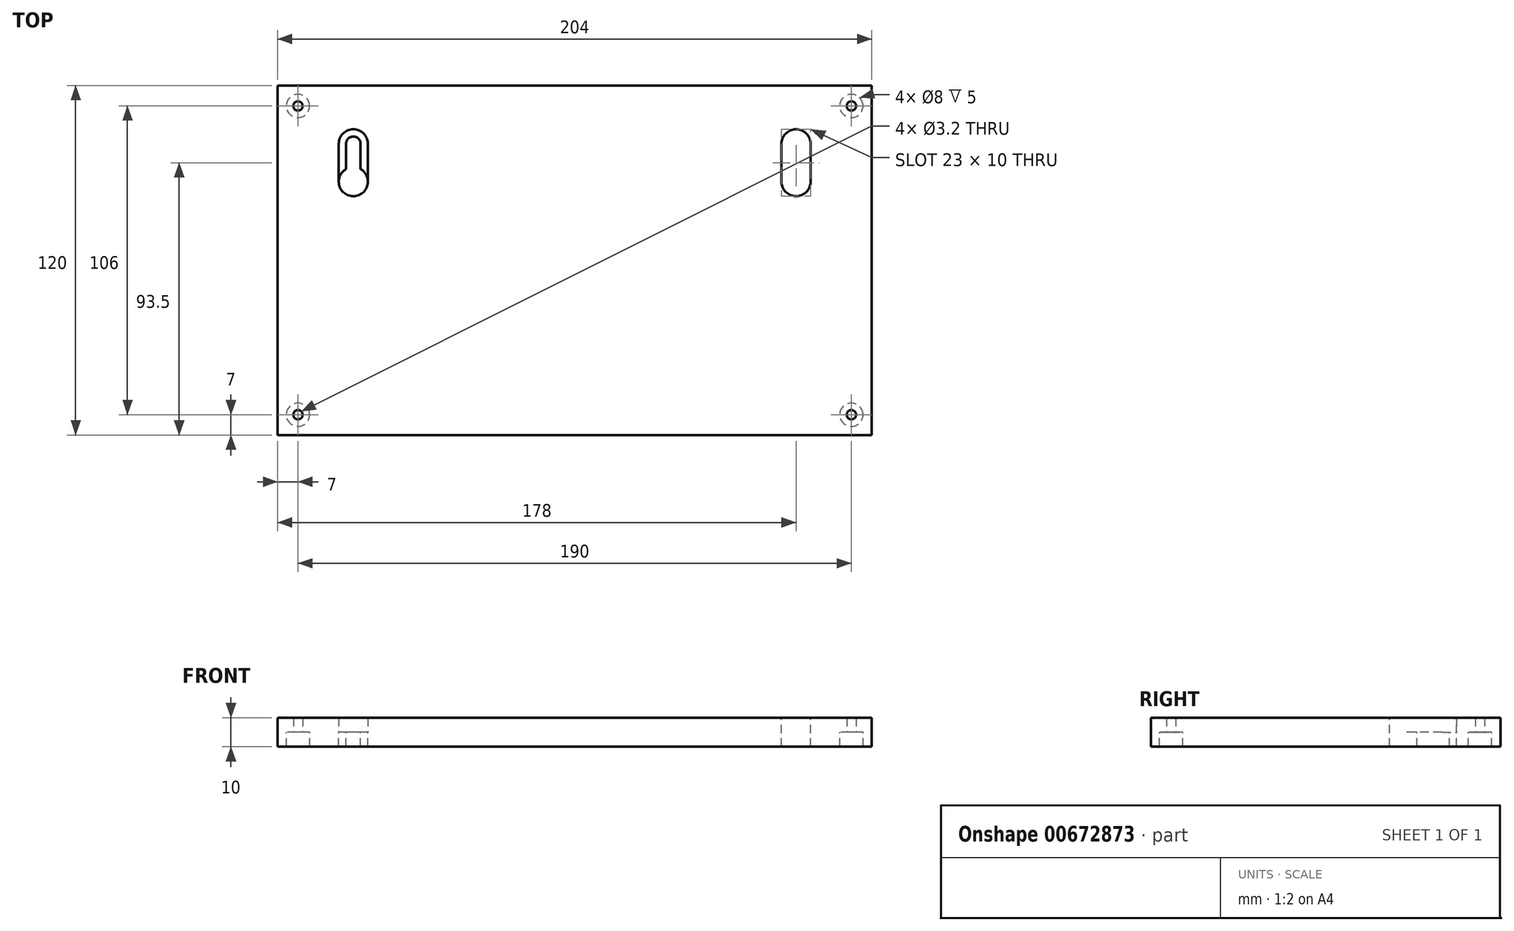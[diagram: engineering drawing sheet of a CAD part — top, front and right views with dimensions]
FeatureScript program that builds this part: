
annotation { "Feature Type Name" : "Feature", "Feature Type Description" : "" }
export const myFeature = defineFeature(function(context is Context, id is Id, definition is map)
    precondition{}
    {
        {
            var Q0;
            Q0=qCreatedBy(makeId("Top.planeOp"),FACE);
            var sketch = newSketch(context, id + "F0", { "sketchPlane" : qUnion([Q0])});
            skLineSegment(sketch, "E0.bottom", {"start": v(102, 60) * mm, "end": v(-102, 60) * mm});
            skLineSegment(sketch, "E0.top", {"start": v(102, -60) * mm, "end": v(-102, -60) * mm});
            skLineSegment(sketch, "E0.left", {"start": v(102, 60) * mm, "end": v(102, -60) * mm});
            skLineSegment(sketch, "E0.right", {"start": v(-102, 60) * mm, "end": v(-102, -60) * mm});
            skPoint(sketch, "E0.middle", {"position": v(0, 0) * mm});
            skArc(sketch, "E1", {"start": v(-71, 40) * mm, "mid": v(-76, 45) * mm, "end": v(-81, 40) * mm});
            skLineSegment(sketch, "E2", {"start": v(-81, 40) * mm, "end": v(-81, 27) * mm});
            skLineSegment(sketch, "E3", {"start": v(-71, 40) * mm, "end": v(-71, 27) * mm});
            skArc(sketch, "E4", {"start": v(-81, 27) * mm, "mid": v(-76, 22) * mm, "end": v(-71, 27) * mm});
            skArc(sketch, "E5", {"start": v(-78.5, 40) * mm, "mid": v(-76, 42.5) * mm, "end": v(-73.5, 40) * mm});
            skArc(sketch, "E6", {"start": v(-71, 27) * mm, "mid": v(-71.67, 29.5) * mm, "end": v(-73.5, 31.33) * mm});
            skLineSegment(sketch, "E7", {"start": v(-78.5, 40) * mm, "end": v(-78.5, 31.33) * mm});
            skLineSegment(sketch, "E8", {"start": v(-73.5, 40) * mm, "end": v(-73.5, 31.33) * mm});
            skArc(sketch, "E9.trimOffspring", {"start": v(-78.5, 31.33) * mm, "mid": v(-80.33, 29.5) * mm, "end": v(-81, 27) * mm});
            skArc(sketch, "E10", {"start": v(71, 40) * mm, "mid": v(76, 45) * mm, "end": v(81, 40) * mm});
            skLineSegment(sketch, "E11", {"start": v(71, 40) * mm, "end": v(71, 27) * mm});
            skLineSegment(sketch, "E12", {"start": v(81, 40) * mm, "end": v(81, 27) * mm});
            skArc(sketch, "E13", {"start": v(71, 27) * mm, "mid": v(76, 22) * mm, "end": v(81, 27) * mm});
            skArc(sketch, "E14", {"start": v(73.5, 40) * mm, "mid": v(76, 42.5) * mm, "end": v(78.5, 40) * mm});
            skArc(sketch, "E15", {"start": v(81, 27) * mm, "mid": v(80.33, 29.5) * mm, "end": v(78.5, 31.33) * mm});
            skLineSegment(sketch, "E16", {"start": v(73.5, 40) * mm, "end": v(73.5, 31.33) * mm});
            skLineSegment(sketch, "E17", {"start": v(78.5, 40) * mm, "end": v(78.5, 31.33) * mm});
            skArc(sketch, "E18.trimOffspring", {"start": v(73.5, 31.33) * mm, "mid": v(71.67, 29.5) * mm, "end": v(71, 27) * mm});
            skLineSegment(sketch, "E19.bottom", {"start": v(102, 60) * mm, "end": v(95, 60) * mm});
            skLineSegment(sketch, "E19.top", {"start": v(96.6, 53) * mm, "end": v(95, 53) * mm});
            skLineSegment(sketch, "E19.left", {"start": v(102, 60) * mm, "end": v(102, 53) * mm});
            skCircle(sketch, "E20", {"center": v(95, 53) * mm, "radius": 4 * mm});
            skCircle(sketch, "E21", {"center": v(95, 53) * mm, "radius": 1.6 * mm});
            skLineSegment(sketch, "E22.bottom", {"start": v(-102, 60) * mm, "end": v(-95, 60) * mm});
            skLineSegment(sketch, "E22.left", {"start": v(-102, 60) * mm, "end": v(-102, 53) * mm});
            skCircle(sketch, "E23", {"center": v(-95, 53) * mm, "radius": 4 * mm});
            skCircle(sketch, "E24", {"center": v(-95, 53) * mm, "radius": 1.6 * mm});
            skLineSegment(sketch, "E25.bottom", {"start": v(-102, -60) * mm, "end": v(-95, -60) * mm});
            skLineSegment(sketch, "E25.left", {"start": v(-102, -60) * mm, "end": v(-102, -53) * mm});
            skCircle(sketch, "E26", {"center": v(-95, -53) * mm, "radius": 4 * mm});
            skCircle(sketch, "E27", {"center": v(-95, -53) * mm, "radius": 1.6 * mm});
            skLineSegment(sketch, "E28.bottom", {"start": v(102, -60) * mm, "end": v(95, -60) * mm});
            skLineSegment(sketch, "E28.left", {"start": v(102, -60) * mm, "end": v(102, -53) * mm});
            skCircle(sketch, "E29", {"center": v(95, -53) * mm, "radius": 4 * mm});
            skCircle(sketch, "E30", {"center": v(95, -53) * mm, "radius": 1.6 * mm});
            skSolve(sketch);
        }
        {
            var Q0;
            Q0=makeQuery(id+"F0.imprint","IMPRINT",FACE,{"disambiguationData":[TD([[makeQuery(id+"F0.imprint","IMPRINT",EDGE,{"derivedFrom":sQuery(id+"F0.wireOp",EDGE,"E0.bottom")}),1.0]])]});
            extrude(context, id + "F1", {"entities" : qUnion([Q0]), "depth" : -5 * mm, "offsetDistance" : 25 * mm});
        }
        {
            var Q0;
            Q0=makeQuery(id+"F0.imprint","IMPRINT",FACE,{"disambiguationData":[TD([[makeQuery(id+"F0.imprint","IMPRINT",EDGE,{"derivedFrom":sQuery(id+"F0.wireOp",EDGE,"E1")}),1.0]])]});
            extrude(context, id + "F2", {"entities" : qUnion([Q0]), "operationType" : NewBodyOperationType.ADD, "depth" : -5 * mm, "offsetDistance" : 25 * mm});
        }
        {
            var Q0;
            Q0=makeQuery(id+"F0.imprint","IMPRINT",FACE,{"disambiguationData":[TD([[makeQuery(id+"F0.imprint","IMPRINT",EDGE,{"derivedFrom":sQuery(id+"F0.wireOp",EDGE,"E0.bottom")}),1.0]])]});
            extrude(context, id + "F3", {"entities" : qUnion([Q0]), "operationType" : NewBodyOperationType.ADD, "depth" : 5 * mm, "offsetDistance" : 25 * mm});
        }
        {
            var Q0;
            Q0=makeQuery(id+"F0.imprint","IMPRINT",FACE,{"disambiguationData":[TD([[makeQuery(id+"F0.imprint","IMPRINT",EDGE,{"derivedFrom":sQuery(id+"F0.wireOp",EDGE,"E29")}),1.0]])]});
            extrude(context, id + "F4", {"entities" : qUnion([Q0]), "operationType" : NewBodyOperationType.ADD, "depth" : 5 * mm, "offsetDistance" : 25 * mm});
        }
        {
            var Q0;
            Q0=makeQuery(id+"F0.imprint","IMPRINT",FACE,{"disambiguationData":[TD([[makeQuery(id+"F0.imprint","IMPRINT",EDGE,{"derivedFrom":sQuery(id+"F0.wireOp",EDGE,"E10")}),-1.0]])]});
            extrude(context, id + "F5", {"entities" : qUnion([Q0]), "operationType" : NewBodyOperationType.ADD, "depth" : -5 * mm, "offsetDistance" : 25 * mm});
        }
        {
            var Q0;
            Q0=makeQuery(id+"F0.imprint","IMPRINT",FACE,{"disambiguationData":[TD([[makeQuery(id+"F0.imprint","IMPRINT",EDGE,{"derivedFrom":sQuery(id+"F0.wireOp",EDGE,"E20")}),1.0]])]});
            extrude(context, id + "F6", {"entities" : qUnion([Q0]), "operationType" : NewBodyOperationType.ADD, "depth" : 5 * mm, "offsetDistance" : 25 * mm});
        }
        {
            var Q0;
            Q0=makeQuery(id+"F0.imprint","IMPRINT",FACE,{"disambiguationData":[TD([[makeQuery(id+"F0.imprint","IMPRINT",EDGE,{"derivedFrom":sQuery(id+"F0.wireOp",EDGE,"E23")}),1.0]])]});
            extrude(context, id + "F7", {"entities" : qUnion([Q0]), "operationType" : NewBodyOperationType.ADD, "depth" : 5 * mm, "offsetDistance" : 25 * mm});
        }
        {
            var Q0;
            Q0=makeQuery(id+"F0.imprint","IMPRINT",FACE,{"disambiguationData":[TD([[makeQuery(id+"F0.imprint","IMPRINT",EDGE,{"derivedFrom":sQuery(id+"F0.wireOp",EDGE,"E26")}),1.0]])]});
            extrude(context, id + "F8", {"entities" : qUnion([Q0]), "operationType" : NewBodyOperationType.ADD, "depth" : 5 * mm, "offsetDistance" : 25 * mm});
        }
    });
